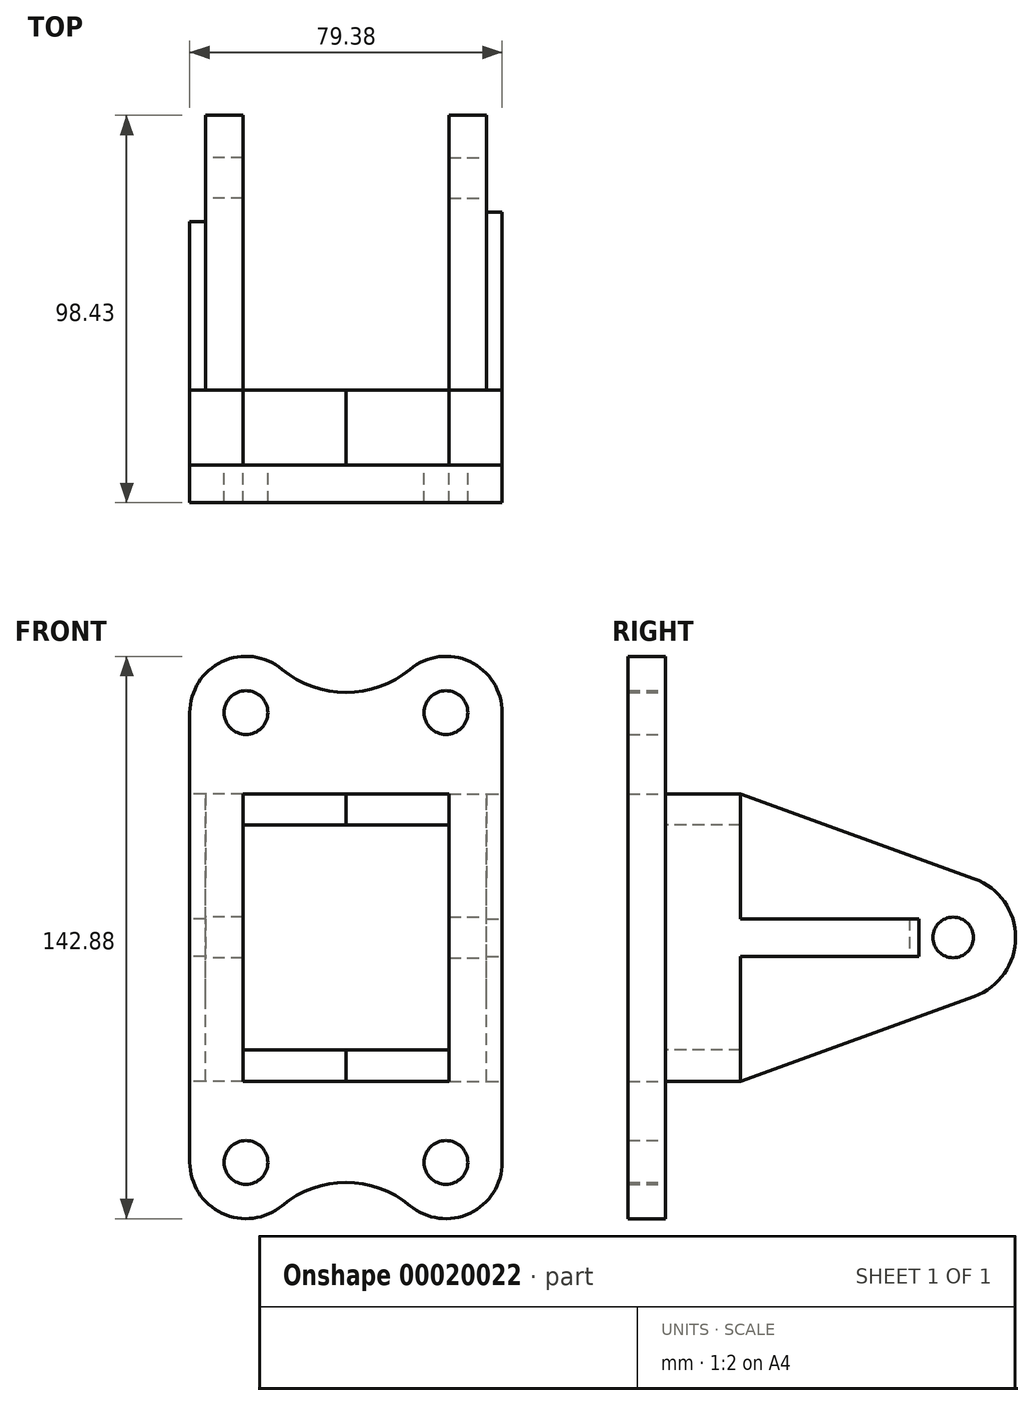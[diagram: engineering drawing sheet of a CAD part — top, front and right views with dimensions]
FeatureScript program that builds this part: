
annotation { "Feature Type Name" : "Feature", "Feature Type Description" : "" }
export const myFeature = defineFeature(function(context is Context, id is Id, definition is map)
    precondition{}
    {
        {
            var Q0;
            Q0=qCreatedBy(makeId("Front.planeOp"),FACE);
            var sketch = newSketch(context, id + "F0", { "sketchPlane" : qUnion([Q0])});
            skArc(sketch, "E0", {"start": v(9.14, 10.98) * mm, "mid": v(-6.06, 12.94) * mm, "end": v(-14.29, 0) * mm});
            skCircle(sketch, "E1", {"center": v(0, 0) * mm, "radius": 5.56 * mm});
            skLineSegment(sketch, "E2", {"start": v(0, 0) * mm, "end": v(-14.29, 0) * mm});
            skLineSegment(sketch, "E3", {"start": v(-14.29, 0) * mm, "end": v(-14.29, -114.3) * mm});
            skLineSegment(sketch, "E4", {"start": v(0, 0) * mm, "end": v(50.8, 0) * mm});
            skCircle(sketch, "E5", {"center": v(50.8, 0) * mm, "radius": 5.56 * mm});
            skArc(sketch, "E6", {"start": v(65.09, 0) * mm, "mid": v(56.86, 12.94) * mm, "end": v(41.66, 10.98) * mm});
            skArc(sketch, "E7", {"start": v(9.14, 10.98) * mm, "mid": v(25.4, 5.1) * mm, "end": v(41.66, 10.98) * mm});
            skLineSegment(sketch, "E8", {"start": v(65.09, 0) * mm, "end": v(65.09, -114.3) * mm});
            skCircle(sketch, "E9", {"center": v(0, -114.3) * mm, "radius": 5.56 * mm});
            skArc(sketch, "E10", {"start": v(-14.29, -114.3) * mm, "mid": v(-6.06, -127.24) * mm, "end": v(9.14, -125.28) * mm});
            skCircle(sketch, "E11", {"center": v(50.8, -114.3) * mm, "radius": 5.56 * mm});
            skArc(sketch, "E12", {"start": v(41.66, -125.28) * mm, "mid": v(56.86, -127.24) * mm, "end": v(65.09, -114.3) * mm});
            skArc(sketch, "E13", {"start": v(41.66, -125.28) * mm, "mid": v(25.4, -119.4) * mm, "end": v(9.14, -125.28) * mm});
            skLineSegment(sketch, "E14.rect.bottom", {"start": v(51.6, -93.66) * mm, "end": v(-0.8, -93.66) * mm});
            skLineSegment(sketch, "E14.rect.top", {"start": v(51.6, -20.64) * mm, "end": v(-0.8, -20.64) * mm});
            skLineSegment(sketch, "E14.rect.left", {"start": v(51.6, -93.66) * mm, "end": v(51.6, -20.64) * mm});
            skLineSegment(sketch, "E14.rect.right", {"start": v(-0.8, -93.66) * mm, "end": v(-0.8, -20.64) * mm});
            skPoint(sketch, "E14.rect.middle", {"position": v(25.4, -57.15) * mm});
            skSolve(sketch);
        }
        {
            var Q0;
            Q0=makeQuery(id+"F0.imprint","IMPRINT",FACE,{"disambiguationData":[TD([[makeQuery(id+"F0.imprint","IMPRINT",EDGE,{"derivedFrom":sQuery(id+"F0.wireOp",EDGE,"E0")}),1.0]])]});
            extrude(context, id + "F1", {"entities" : qUnion([Q0]), "depth" : 9.52 * mm});
        }
        {
            var Q0;
            Q0=makeQuery(id+"F1.opExtrude","SWEPT_FACE",FACE,{"disambiguationData":[OSD([sQuery(id+"F0.wireOp",EDGE,"E8")])]});
            var sketch = newSketch(context, id + "F2", { "sketchPlane" : qUnion([Q0])});
            skLineSegment(sketch, "E15", {"start": v(-9.53, 0) * mm, "end": v(-9.53, -57.15) * mm});
            skLineSegment(sketch, "E16", {"start": v(-9.52, -57.15) * mm, "end": v(73.03, -57.15) * mm, "construction": true});
            skCircle(sketch, "E17", {"center": v(73.03, -57.15) * mm, "radius": 5.16 * mm});
            skLineSegment(sketch, "E18", {"start": v(73.03, -57.15) * mm, "end": v(64.3, -57.15) * mm, "construction": true});
            skLineSegment(sketch, "E19", {"start": v(64.3, -57.15) * mm, "end": v(64.3, -52.39) * mm});
            skLineSegment(sketch, "E20", {"start": v(64.3, -57.15) * mm, "end": v(64.3, -61.91) * mm});
            skLineSegment(sketch, "E21", {"start": v(64.3, -61.91) * mm, "end": v(19.05, -61.91) * mm});
            skLineSegment(sketch, "E22", {"start": v(64.3, -52.39) * mm, "end": v(19.05, -52.39) * mm});
            skPoint(sketch, "E23.orphan", {"position": v(0, -61.91) * mm});
            skPoint(sketch, "E24.orphan", {"position": v(0, -52.39) * mm});
            skLineSegment(sketch, "E25", {"start": v(19.05, -93.66) * mm, "end": v(0, -93.66) * mm});
            skLineSegment(sketch, "E26", {"start": v(19.05, -20.64) * mm, "end": v(0, -20.64) * mm});
            skLineSegment(sketch, "E27", {"start": v(0, -93.66) * mm, "end": v(19.05, -93.66) * mm});
            skLineSegment(sketch, "E28", {"start": v(19.05, -93.66) * mm, "end": v(19.05, -61.91) * mm});
            skLineSegment(sketch, "E29", {"start": v(19.05, -52.39) * mm, "end": v(19.05, -20.64) * mm});
            skLineSegment(sketch, "E30", {"start": v(19.05, -93.66) * mm, "end": v(78.45, -72.07) * mm});
            skLineSegment(sketch, "E31", {"start": v(19.05, -20.64) * mm, "end": v(78.45, -42.23) * mm});
            skLineSegment(sketch, "E32", {"start": v(19.05, -20.64) * mm, "end": v(19.05, -57.15) * mm});
            skLineSegment(sketch, "E33", {"start": v(19.05, -57.15) * mm, "end": v(19.05, -93.66) * mm});
            skArc(sketch, "E34.trimOffspring", {"start": v(78.45, -72.07) * mm, "mid": v(88.9, -57.15) * mm, "end": v(78.45, -42.23) * mm});
            skSolve(sketch);
        }
        {
            var Q0;
            Q0=makeQuery(id+"F2.imprint","IMPRINT",FACE,{"disambiguationData":[TD([[makeQuery(id+"F2.imprint","IMPRINT",EDGE,{"derivedFrom":sQuery(id+"F2.wireOp",EDGE,"E17")}),-1.0]])]});
            var Q1;
            {var subQ2=sQuery(id+"F2.wireOp",EDGE,"E26");Q1=makeQuery(id+"F2.imprint","IMPRINT",FACE,{"disambiguationData":[TD([[makeQuery(id+"F2.imprint","IMPRINT",EDGE,{"derivedFrom":subQ2}),1.0]])]});}
            var Q2;
            Q2=makeQuery(id+"F2.imprint","IMPRINT",FACE,{"disambiguationData":[TD([[makeQuery(id+"F2.imprint","IMPRINT",EDGE,{"derivedFrom":sQuery(id+"F2.wireOp",EDGE,"E19")}),1.0]])]});
            extrude(context, id + "F3", {"entities" : qUnion([Q0, Q1, Q2]), "oppositeDirection" : true, "depth" : 13.5 * mm});
        }
        {
            var Q0;
            Q0=makeQuery(id+"F2.imprint","IMPRINT",FACE,{"disambiguationData":[TD([[makeQuery(id+"F2.imprint","IMPRINT",EDGE,{"derivedFrom":sQuery(id+"F2.wireOp",EDGE,"E17")}),-1.0]])]});
            extrude(context, id + "F4", {"entities" : qUnion([Q0]), "operationType" : NewBodyOperationType.REMOVE, "oppositeDirection" : true, "depth" : 3.97 * mm});
        }
        {
            var Q0;
            Q0=makeQuery(id+"F3.boolean.opBoolean","MERGE",FACE,{"derivedFrom":[makeQuery(id+"F1.opExtrude","SWEPT_FACE",FACE,{"disambiguationData":[OSD([sQuery(id+"F0.wireOp",EDGE,"E14.rect.left")])]}),makeQuery(id+"F3.opExtrude","CAP_FACE",FACE,{"disambiguationData":[OSD([sQuery(id+"F0.wireOp",EDGE,"E8"),sQuery(id+"F2.wireOp",EDGE,"E17"),sQuery(id+"F2.wireOp",EDGE,"E26"),sQuery(id+"F2.wireOp",EDGE,"E27"),sQuery(id+"F2.wireOp",EDGE,"E30"),sQuery(id+"F2.wireOp",EDGE,"E31"),sQuery(id+"F2.wireOp",EDGE,"E34.trimOffspring")])],"isStart":false})]});
            var sketch = newSketch(context, id + "F5", { "sketchPlane" : qUnion([Q0])});
            skLineSegment(sketch, "E35", {"start": v(-19.05, -93.66) * mm, "end": v(-19.05, -85.72) * mm});
            skLineSegment(sketch, "E36", {"start": v(-19.05, -85.72) * mm, "end": v(9.52, -85.72) * mm});
            skLineSegment(sketch, "E37", {"start": v(-19.05, -20.64) * mm, "end": v(-19.05, -28.57) * mm});
            skLineSegment(sketch, "E38", {"start": v(-19.05, -28.57) * mm, "end": v(9.52, -28.57) * mm});
            skLineSegment(sketch, "E39", {"start": v(9.52, -28.57) * mm, "end": v(9.52, -20.64) * mm});
            skLineSegment(sketch, "E40", {"start": v(9.52, -20.64) * mm, "end": v(-19.05, -20.64) * mm});
            skLineSegment(sketch, "E41", {"start": v(-19.05, -93.66) * mm, "end": v(9.52, -93.66) * mm});
            skLineSegment(sketch, "E42", {"start": v(9.52, -93.66) * mm, "end": v(9.52, -85.72) * mm});
            skSolve(sketch);
        }
        {
            var Q0;
            Q0=makeQuery(id+"F5.imprint","IMPRINT",FACE,{"disambiguationData":[TD([[makeQuery(id+"F5.imprint","IMPRINT",EDGE,{"derivedFrom":sQuery(id+"F5.wireOp",EDGE,"E37")}),1.0]])]});
            var Q1;
            Q1=makeQuery(id+"F5.imprint","IMPRINT",FACE,{"disambiguationData":[TD([[makeQuery(id+"F5.imprint","IMPRINT",EDGE,{"derivedFrom":sQuery(id+"F5.wireOp",EDGE,"E35")}),-1.0]])]});
            extrude(context, id + "F6", {"entities" : qUnion([Q0, Q1]), "depth" : 26.2 * mm});
        }
        {
            var Q0;
            Q0=makeQuery(id+"F5.imprint","IMPRINT",FACE,{"disambiguationData":[TD([[makeQuery(id+"F5.imprint","IMPRINT",EDGE,{"derivedFrom":sQuery(id+"F5.wireOp",EDGE,"E37")}),1.0]])]});
            var Q1;
            Q1=makeQuery(id+"F5.imprint","IMPRINT",FACE,{"disambiguationData":[TD([[makeQuery(id+"F5.imprint","IMPRINT",EDGE,{"derivedFrom":sQuery(id+"F5.wireOp",EDGE,"E35")}),-1.0]])]});
            extrude(context, id + "F7", {"entities" : qUnion([Q0, Q1]), "depth" : 26.2 * mm});
        }
        {
            var Q0;
            Q0=makeQuery(id+"F2.imprint","IMPRINT",FACE,{"disambiguationData":[TD([[makeQuery(id+"F2.imprint","IMPRINT",EDGE,{"derivedFrom":sQuery(id+"F2.wireOp",EDGE,"E17")}),-1.0]])]});
            extrude(context, id + "F8", {"entities" : qUnion([Q0]), "operationType" : NewBodyOperationType.REMOVE, "oppositeDirection" : true, "depth" : 3.97 * mm});
        }
        {
            var Q0;
            Q0=qCreatedBy(makeId("Right.planeOp"),FACE);
            cPlane(context, id + "F9", {"entities" : qUnion([Q0]), "cplaneType" : CPlaneType.OFFSET, "offset" : 25.4 * mm, "width" : 152.4 * mm, "height" : 152.4 * mm});
        }
        {
            var Q0;
            Q0=makeQuery(id+"F6.opExtrude","SWEPT_BODY",BODY,{"disambiguationData":[OSD([sQuery(id+"F5.wireOp",EDGE,"E37"),sQuery(id+"F5.wireOp",EDGE,"E38"),sQuery(id+"F5.wireOp",EDGE,"E39"),sQuery(id+"F5.wireOp",EDGE,"E40")])]});
            var Q1;
            Q1=makeQuery(id+"F3.opExtrude","SWEPT_BODY",BODY,{"disambiguationData":[OSD([sQuery(id+"F0.wireOp",EDGE,"E8"),sQuery(id+"F2.wireOp",EDGE,"E17"),sQuery(id+"F2.wireOp",EDGE,"E26"),sQuery(id+"F2.wireOp",EDGE,"E27"),sQuery(id+"F2.wireOp",EDGE,"E30"),sQuery(id+"F2.wireOp",EDGE,"E31"),sQuery(id+"F2.wireOp",EDGE,"E34.trimOffspring")])]});
            var Q2;
            Q2=makeQuery(id+"F7.opExtrude","SWEPT_BODY",BODY,{"disambiguationData":[OSD([sQuery(id+"F5.wireOp",EDGE,"E35"),sQuery(id+"F5.wireOp",EDGE,"E36"),sQuery(id+"F5.wireOp",EDGE,"E41"),sQuery(id+"F5.wireOp",EDGE,"E42")])]});
            var Q3;
            Q3=qCreatedBy(id+"F9.planeOp",FACE);
            mirror(context, id + "F10", {"entities" : qUnion([Q0, Q1, Q2]), "mirrorPlane" : qUnion([Q3])});
        }
        {
            var Q0;
            Q0=makeQuery(id+"F10.opPattern","COPY",FACE,{"derivedFrom":makeQuery(id+"F3.opExtrude","CAP_FACE",FACE,{"disambiguationData":[OSD([sQuery(id+"F0.wireOp",EDGE,"E8"),sQuery(id+"F2.wireOp",EDGE,"E17"),sQuery(id+"F2.wireOp",EDGE,"E26"),sQuery(id+"F2.wireOp",EDGE,"E27"),sQuery(id+"F2.wireOp",EDGE,"E30"),sQuery(id+"F2.wireOp",EDGE,"E31"),sQuery(id+"F2.wireOp",EDGE,"E34.trimOffspring")])],"isStart":true}),"instanceName":"1"});
            var sketch = newSketch(context, id + "F11", { "sketchPlane" : qUnion([Q0])});
            skLineSegment(sketch, "E43", {"start": v(-64.3, -52.39) * mm, "end": v(-61.91, -52.39) * mm});
            skLineSegment(sketch, "E44", {"start": v(-61.91, -52.39) * mm, "end": v(-61.91, -61.91) * mm});
            skLineSegment(sketch, "E45", {"start": v(-61.91, -61.91) * mm, "end": v(-64.3, -61.91) * mm});
            skLineSegment(sketch, "E46", {"start": v(-64.3, -61.91) * mm, "end": v(-64.3, -52.39) * mm});
            skSolve(sketch);
        }
        {
            var Q0;
            Q0 = qSketchRegion(id + "F11", true);
            extrude(context, id + "F12", {"entities" : qUnion([Q0]), "operationType" : NewBodyOperationType.REMOVE, "oppositeDirection" : true, "depth" : 3.97 * mm});
        }
    });
